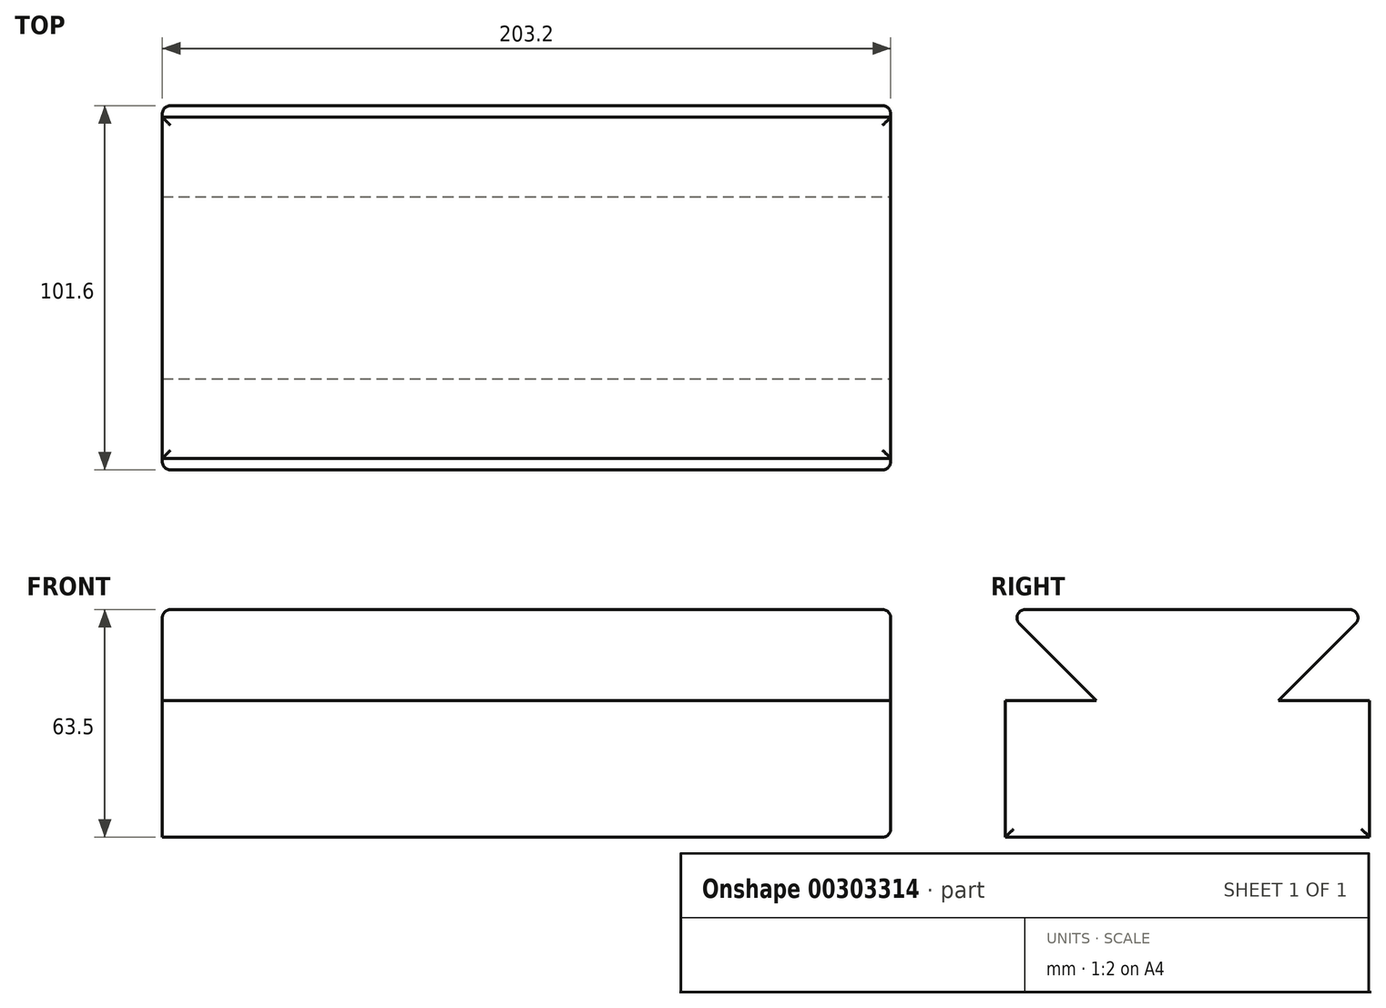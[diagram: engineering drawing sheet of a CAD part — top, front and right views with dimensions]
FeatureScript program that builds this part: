
annotation { "Feature Type Name" : "Feature", "Feature Type Description" : "" }
export const myFeature = defineFeature(function(context is Context, id is Id, definition is map)
    precondition{}
    {
        {
            var Q0;
            Q0=qCreatedBy(makeId("Top.planeOp"),FACE);
            var sketch = newSketch(context, id + "F0", { "sketchPlane" : qUnion([Q0])});
            skLineSegment(sketch, "E0.bottom", {"start": v(0, 0) * mm, "end": v(203.2, 0) * mm});
            skLineSegment(sketch, "E0.top", {"start": v(0, 101.6) * mm, "end": v(203.2, 101.6) * mm});
            skLineSegment(sketch, "E0.left", {"start": v(0, 0) * mm, "end": v(0, 101.6) * mm});
            skLineSegment(sketch, "E0.right", {"start": v(203.2, 0) * mm, "end": v(203.2, 101.6) * mm});
            skSolve(sketch);
        }
        {
            var Q0;
            Q0=makeQuery(id+"F0.imprint","IMPRINT",FACE,{"disambiguationData":[TD([[makeQuery(id+"F0.imprint","IMPRINT",EDGE,{"derivedFrom":sQuery(id+"F0.wireOp",EDGE,"E0.bottom")}),1.0]])]});
            extrude(context, id + "F1", {"entities" : qUnion([Q0]), "depth" : 63.5 * mm});
        }
        {
            var Q0;
            Q0=makeQuery(id+"F1.opExtrude","SWEPT_FACE",FACE,{"disambiguationData":[OSD([sQuery(id+"F0.wireOp",EDGE,"E0.right")])]});
            var sketch = newSketch(context, id + "F2", { "sketchPlane" : qUnion([Q0])});
            skLineSegment(sketch, "E1", {"start": v(0, 63.5) * mm, "end": v(25.4, 38.1) * mm});
            skLineSegment(sketch, "E2", {"start": v(0, 38.1) * mm, "end": v(25.4, 38.1) * mm});
            skLineSegment(sketch, "E3", {"start": v(101.6, 63.5) * mm, "end": v(76.2, 38.1) * mm});
            skLineSegment(sketch, "E4", {"start": v(76.2, 38.1) * mm, "end": v(101.6, 38.1) * mm});
            skSolve(sketch);
        }
        {
            var Q0;
            {var subQ0=sQuery(id+"F2.wireOp",EDGE,"E1");Q0=makeQuery(id+"F2.imprint","IMPRINT",FACE,{"disambiguationData":[TD([[makeQuery(id+"F2.imprint","IMPRINT",EDGE,{"derivedFrom":subQ0}),-1.0]])]});}
            var Q1;
            {var subQ0=sQuery(id+"F2.wireOp",EDGE,"E3");Q1=makeQuery(id+"F2.imprint","IMPRINT",FACE,{"disambiguationData":[TD([[makeQuery(id+"F2.imprint","IMPRINT",EDGE,{"derivedFrom":subQ0}),1.0]])]});}
            extrude(context, id + "F3", {"entities" : qUnion([Q0, Q1]), "operationType" : NewBodyOperationType.REMOVE, "endBound" : BoundingType.UP_TO_NEXT, "oppositeDirection" : true, "depth" : 25.4 * mm});
        }
        {
            var Q0;
            Q0=makeQuery(id+"F1.opExtrude","CAP_EDGE",EDGE,{"disambiguationData":[OSD([sQuery(id+"F0.wireOp",EDGE,"E0.right")])],"isStart":false});
            var Q1;
            Q1=makeQuery(id+"F3.boolean.opBoolean","COPY",EDGE,{"derivedFrom":makeQuery(id+"F3.opExtrude","CAP_EDGE",EDGE,{"disambiguationData":[OSD([sQuery(id+"F2.wireOp",EDGE,"E1")])],"isStart":true})});
            var Q2;
            Q2=makeQuery(id+"F3.boolean.opBoolean","COPY",EDGE,{"derivedFrom":makeQuery(id+"F3.opExtrude","CAP_EDGE",EDGE,{"disambiguationData":[OSD([sQuery(id+"F2.wireOp",EDGE,"E2")])],"isStart":true})});
            var Q3;
            Q3=makeQuery(id+"F1.opExtrude","SWEPT_EDGE",EDGE,{"disambiguationData":[OSD([sQuery(id+"F0.wireOp",EDGE,"E0.bottom"),sQuery(id+"F0.wireOp",EDGE,"E0.right")])]});
            var Q4;
            Q4=makeQuery(id+"F1.opExtrude","CAP_EDGE",EDGE,{"disambiguationData":[OSD([sQuery(id+"F0.wireOp",EDGE,"E0.right")])],"isStart":true});
            var Q5;
            Q5=makeQuery(id+"F1.opExtrude","SWEPT_EDGE",EDGE,{"disambiguationData":[OSD([sQuery(id+"F0.wireOp",EDGE,"E0.top"),sQuery(id+"F0.wireOp",EDGE,"E0.right")])]});
            var Q6;
            Q6=makeQuery(id+"F3.boolean.opBoolean","COPY",EDGE,{"derivedFrom":makeQuery(id+"F3.opExtrude","CAP_EDGE",EDGE,{"disambiguationData":[OSD([sQuery(id+"F2.wireOp",EDGE,"E4")])],"isStart":true})});
            var Q7;
            Q7=makeQuery(id+"F3.boolean.opBoolean","COPY",EDGE,{"derivedFrom":makeQuery(id+"F3.opExtrude","CAP_EDGE",EDGE,{"disambiguationData":[OSD([sQuery(id+"F2.wireOp",EDGE,"E3")])],"isStart":true})});
            var Q8;
            Q8=makeQuery(id+"F3.boolean.opBoolean","COPY",EDGE,{"derivedFrom":makeQuery(id+"F3.opExtrude","SWEPT_EDGE",EDGE,{"disambiguationData":[OSD([sQuery(id+"F0.wireOp",EDGE,"E0.bottom"),sQuery(id+"F0.wireOp",EDGE,"E0.right"),sQuery(id+"F2.wireOp",EDGE,"E2")])]})});
            var Q9;
            {var subQ0=sQuery(id+"F0.wireOp",EDGE,"E0.bottom");Q9=makeQuery(id+"F3.boolean.opBoolean","MERGE",EDGE,{"derivedFrom":[makeQuery(id+"F1.opExtrude","CAP_EDGE",EDGE,{"disambiguationData":[OSD([subQ0])],"isStart":false})],"fromTools":[makeQuery(id+"F3.opExtrude","SWEPT_EDGE",EDGE,{"disambiguationData":[OSD([subQ0,sQuery(id+"F0.wireOp",EDGE,"E0.right"),sQuery(id+"F2.wireOp",EDGE,"E1")])]})]});}
            var Q10;
            Q10=makeQuery(id+"F1.opExtrude","SWEPT_EDGE",EDGE,{"disambiguationData":[OSD([sQuery(id+"F0.wireOp",EDGE,"E0.bottom"),sQuery(id+"F0.wireOp",EDGE,"E0.left")])]});
            var Q11;
            Q11=makeQuery(id+"F3.boolean.opBoolean","COPY",EDGE,{"derivedFrom":makeQuery(id+"F3.opExtrude","CAP_EDGE",EDGE,{"disambiguationData":[OSD([sQuery(id+"F2.wireOp",EDGE,"E2")])],"isStart":false})});
            var Q12;
            Q12=makeQuery(id+"F3.boolean.opBoolean","COPY",EDGE,{"derivedFrom":makeQuery(id+"F3.opExtrude","CAP_EDGE",EDGE,{"disambiguationData":[OSD([sQuery(id+"F2.wireOp",EDGE,"E1")])],"isStart":false})});
            var Q13;
            Q13=makeQuery(id+"F1.opExtrude","CAP_EDGE",EDGE,{"disambiguationData":[OSD([sQuery(id+"F0.wireOp",EDGE,"E0.left")])],"isStart":false});
            var Q14;
            Q14=makeQuery(id+"F3.boolean.opBoolean","COPY",EDGE,{"derivedFrom":makeQuery(id+"F3.opExtrude","CAP_EDGE",EDGE,{"disambiguationData":[OSD([sQuery(id+"F2.wireOp",EDGE,"E3")])],"isStart":false})});
            var Q15;
            Q15=makeQuery(id+"F3.boolean.opBoolean","COPY",EDGE,{"derivedFrom":makeQuery(id+"F3.opExtrude","CAP_EDGE",EDGE,{"disambiguationData":[OSD([sQuery(id+"F2.wireOp",EDGE,"E4")])],"isStart":false})});
            var Q16;
            Q16=makeQuery(id+"F1.opExtrude","SWEPT_EDGE",EDGE,{"disambiguationData":[OSD([sQuery(id+"F0.wireOp",EDGE,"E0.top"),sQuery(id+"F0.wireOp",EDGE,"E0.left")])]});
            var Q17;
            Q17=makeQuery(id+"F3.boolean.opBoolean","COPY",EDGE,{"derivedFrom":makeQuery(id+"F3.opExtrude","SWEPT_EDGE",EDGE,{"disambiguationData":[OSD([sQuery(id+"F0.wireOp",EDGE,"E0.top"),sQuery(id+"F0.wireOp",EDGE,"E0.right"),sQuery(id+"F2.wireOp",EDGE,"E4")])]})});
            var Q18;
            {var subQ0=sQuery(id+"F0.wireOp",EDGE,"E0.top");Q18=makeQuery(id+"F3.boolean.opBoolean","MERGE",EDGE,{"derivedFrom":[makeQuery(id+"F1.opExtrude","CAP_EDGE",EDGE,{"disambiguationData":[OSD([subQ0])],"isStart":false})],"fromTools":[makeQuery(id+"F3.opExtrude","SWEPT_EDGE",EDGE,{"disambiguationData":[OSD([subQ0,sQuery(id+"F0.wireOp",EDGE,"E0.right"),sQuery(id+"F2.wireOp",EDGE,"E3")])]})]});}
            fillet(context, id + "F4", {"entities" : qUnion([Q0, Q1, Q2, Q3, Q4, Q5, Q6, Q7, Q8, Q9, Q10, Q11, Q12, Q13, Q14, Q15, Q16, Q17, Q18]), "radius" : 2.3 * mm, "tangentPropagation" : true, "allowEdgeOverflow" : false});
        }
    });
